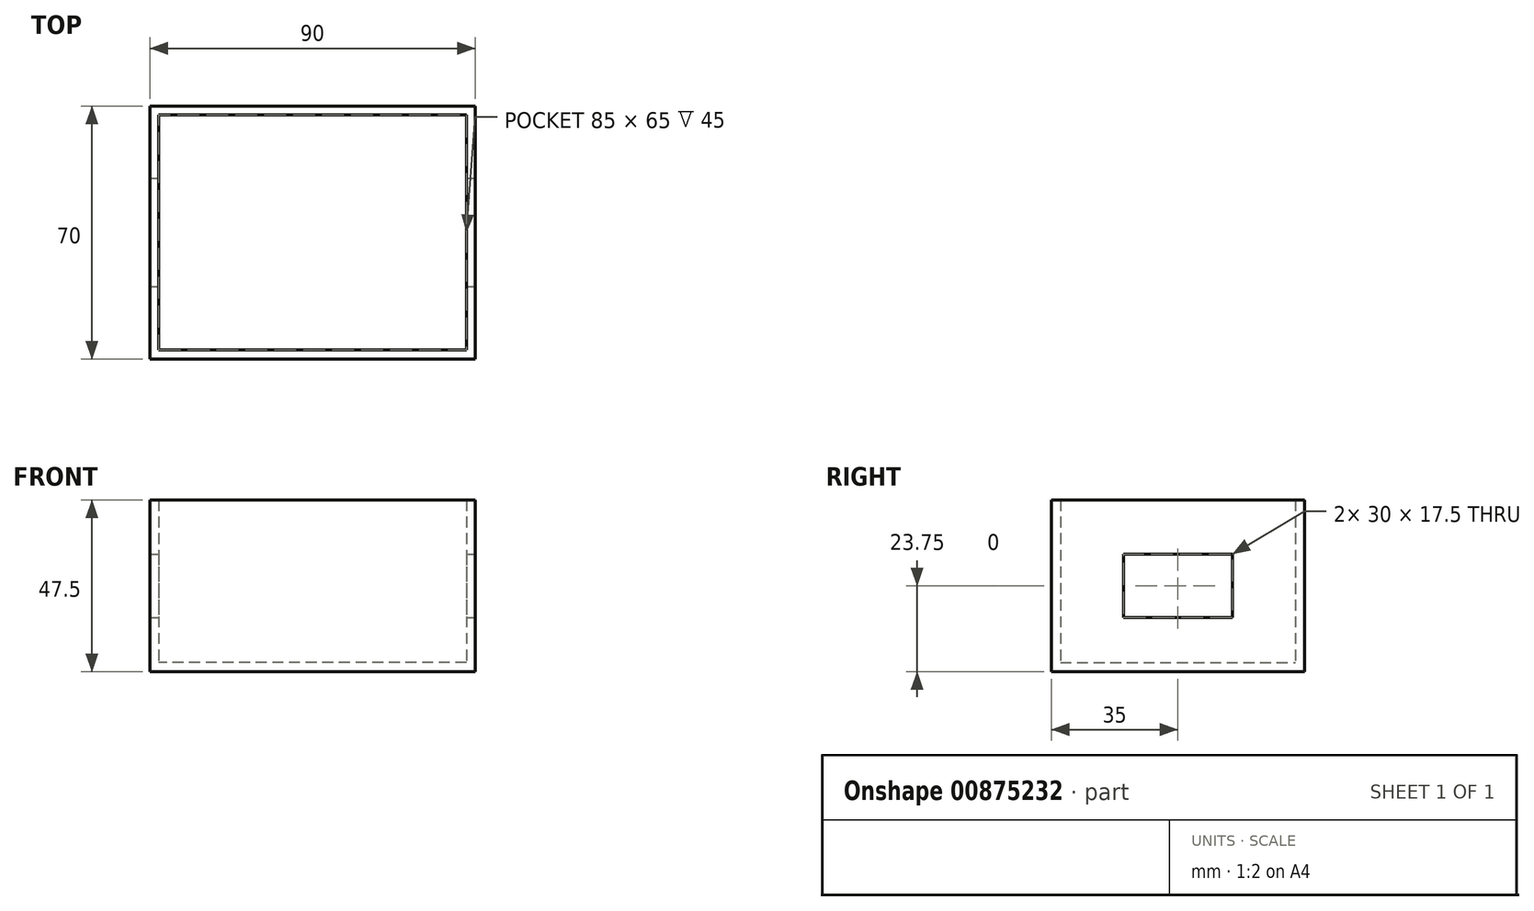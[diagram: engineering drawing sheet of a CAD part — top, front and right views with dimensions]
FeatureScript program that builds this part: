
annotation { "Feature Type Name" : "Feature", "Feature Type Description" : "" }
export const myFeature = defineFeature(function(context is Context, id is Id, definition is map)
    precondition{}
    {
        {
            var Q0;
            Q0=qCreatedBy(makeId("Top.planeOp"),FACE);
            var sketch = newSketch(context, id + "F0", { "sketchPlane" : qUnion([Q0])});
            skLineSegment(sketch, "E0.bottom", {"start": v(45, -35) * mm, "end": v(-45, -35) * mm});
            skLineSegment(sketch, "E0.top", {"start": v(45, 35) * mm, "end": v(-45, 35) * mm});
            skLineSegment(sketch, "E0.left", {"start": v(45, -35) * mm, "end": v(45, 35) * mm});
            skLineSegment(sketch, "E0.right", {"start": v(-45, -35) * mm, "end": v(-45, 35) * mm});
            skPoint(sketch, "E0.middle", {"position": v(0, 0) * mm});
            skSolve(sketch);
        }
        {
            var Q0;
            Q0 = qSketchRegion(id + "F0", true);
            extrude(context, id + "F1", {"entities" : qUnion([Q0]), "depth" : 47.5 * mm, "offsetDistance" : 25 * mm});
        }
        {
            var Q0;
            Q0=makeQuery(id+"F1.opExtrude","CAP_FACE",FACE,{"disambiguationData":[OSD([sQuery(id+"F0.wireOp",EDGE,"E0.bottom"),sQuery(id+"F0.wireOp",EDGE,"E0.top"),sQuery(id+"F0.wireOp",EDGE,"E0.left"),sQuery(id+"F0.wireOp",EDGE,"E0.right")])],"isStart":false});
            shell(context, id + "F2", {"entities" : qUnion([Q0]), "thickness" : 2.5 * mm});
        }
        {
            var Q0;
            Q0=makeQuery(id+"F1.opExtrude","SWEPT_FACE",FACE,{"disambiguationData":[OSD([sQuery(id+"F0.wireOp",EDGE,"E0.left")])]});
            var sketch = newSketch(context, id + "F3", { "sketchPlane" : qUnion([Q0])});
            skLineSegment(sketch, "E1.bottom", {"start": v(15, 15) * mm, "end": v(-15, 15) * mm});
            skLineSegment(sketch, "E1.top", {"start": v(15, 32.5) * mm, "end": v(-15, 32.5) * mm});
            skLineSegment(sketch, "E1.left", {"start": v(15, 15) * mm, "end": v(15, 32.5) * mm});
            skLineSegment(sketch, "E1.right", {"start": v(-15, 15) * mm, "end": v(-15, 32.5) * mm});
            skPoint(sketch, "E1.middle", {"position": v(0, 23.75) * mm});
            skSolve(sketch);
        }
        {
            var Q0;
            Q0=makeQuery(id+"F3.imprint","IMPRINT",FACE,{"disambiguationData":[TD([[makeQuery(id+"F3.imprint","IMPRINT",EDGE,{"derivedFrom":sQuery(id+"F3.wireOp",EDGE,"E1.bottom")}),-1.0]])]});
            var Q1;
            Q1=makeQuery(id+"F1.opExtrude","SWEPT_FACE",FACE,{"disambiguationData":[OSD([sQuery(id+"F0.wireOp",EDGE,"E0.right")])]});
            extrude(context, id + "F4", {"entities" : qUnion([Q0]), "operationType" : NewBodyOperationType.REMOVE, "endBound" : BoundingType.UP_TO_SURFACE, "oppositeDirection" : true, "depth" : 90.6 * mm, "endBoundEntityFace" : qUnion([Q1]), "offsetDistance" : 25 * mm});
        }
    });
